# Revit family: Armor X2-2014
name_source: partatom
category: Mechanical Equipment
revit_build: Autodesk Revit 2014 (Build: 20130308_1515(x64)
units: mm (PartAtom-declared; Revit-internal decimal feet)

## types (3) — shared parameters
# of Electrical Connections = 1
Description = ARMOR X2 CONDENSING WATER HEATER
FUEL TYPE = NATURAL GAS
Fuel Type = Natural or LP
HEIGHT = 58 3/4"
Manufacturer = Lochinvar
RECOVERY (GPH) = (based on temperature rise - see product data)
Total Amps = 5.5
Voltage/Control = 24
Voltage/Heater = 120
WIDTH = 31"

## per-type parameters (varying)
| type | DEPTH | GALLON CAPACITY | INPUT RATE (BTUH) | Total Amps-Heater and Pumps | URL |
| AWN1000PM | 48" | 8.4 | 999,999 | 16.9 | http://www.lochinvar.com |
| AWN1300PM | 52 1/4" | 10.0 | 1.300.000 | 24.7 | http://Lochinvar.com |
| AWN1500PM | 56 1/2" | 11.4 | 1,500,000 | 24.7 | http://www.lochinvar.com |

note: column(s) folded — value = type name in every type: MODEL NO., Model

## geometry (parser evidence)
native form markers: Sweep x4
no freeform markers — native parametric forms only
